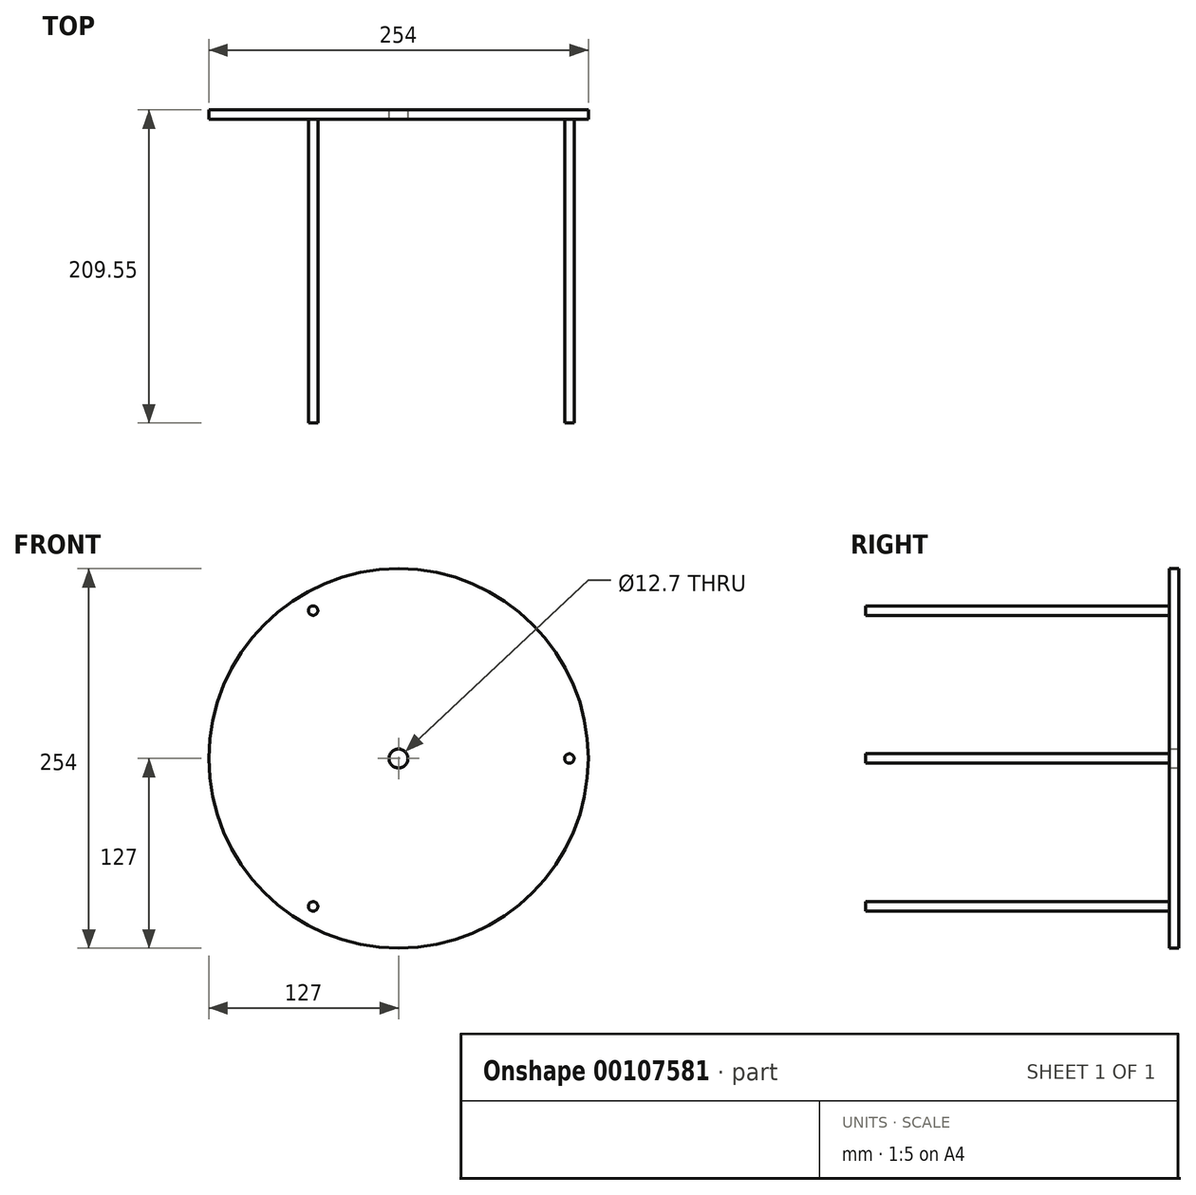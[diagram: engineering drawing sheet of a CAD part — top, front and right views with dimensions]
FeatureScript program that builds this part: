
annotation { "Feature Type Name" : "Feature", "Feature Type Description" : "" }
export const myFeature = defineFeature(function(context is Context, id is Id, definition is map)
    precondition{}
    {
        {
            var Q0;
            Q0=qCreatedBy(makeId("Front.planeOp"),FACE);
            var sketch = newSketch(context, id + "F0", { "sketchPlane" : qUnion([Q0])});
            skCircle(sketch, "E0", {"center": v(0, 0) * mm, "radius": 127 * mm});
            skCircle(sketch, "E1", {"center": v(0, 0) * mm, "radius": 6.35 * mm});
            skSolve(sketch);
        }
        {
            var Q0;
            Q0 = qSketchRegion(id + "F0", true);
            extrude(context, id + "F1", {"entities" : qUnion([Q0]), "depth" : 6.35 * mm});
        }
        {
            var Q0;
            Q0=makeQuery(id+"F1.opExtrude","CAP_FACE",FACE,{"disambiguationData":[OSD([sQuery(id+"F0.wireOp",EDGE,"E0"),sQuery(id+"F0.wireOp",EDGE,"E1")])],"isStart":false});
            var sketch = newSketch(context, id + "F2", { "sketchPlane" : qUnion([Q0])});
            skCircle(sketch, "E2", {"center": v(0, 0) * mm, "radius": 114.3 * mm, "construction": true});
            skCircle(sketch, "E3", {"center": v(114.3, 0) * mm, "radius": 3.18 * mm});
            skCircle(sketch, "E4.1.0", {"center": v(-57.15, 98.99) * mm, "radius": 3.18 * mm});
            skCircle(sketch, "E4.2.0", {"center": v(-57.15, -98.99) * mm, "radius": 3.18 * mm});
            skSolve(sketch);
        }
        {
            var Q0;
            Q0 = qSketchRegion(id + "F2", true);
            extrude(context, id + "F3", {"entities" : qUnion([Q0]), "operationType" : NewBodyOperationType.ADD, "depth" : 203.2 * mm});
        }
    });
